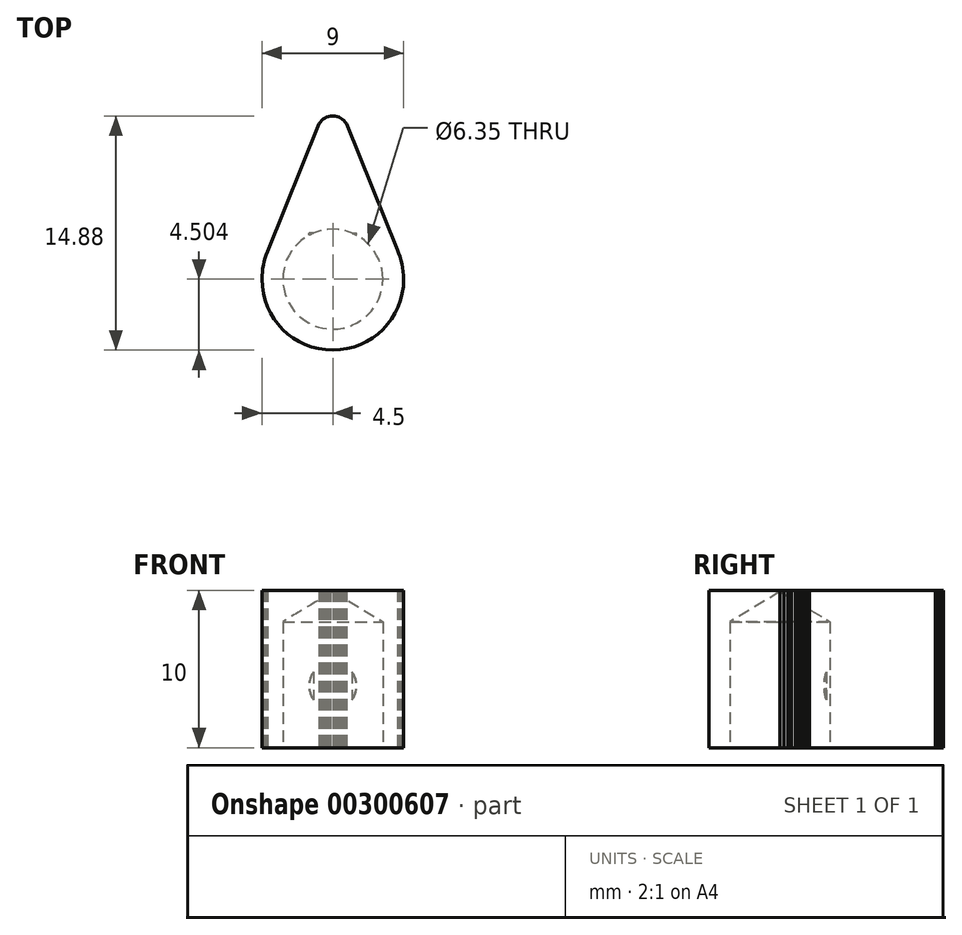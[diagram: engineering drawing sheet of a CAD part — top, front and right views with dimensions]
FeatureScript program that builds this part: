
annotation { "Feature Type Name" : "Feature", "Feature Type Description" : "" }
export const myFeature = defineFeature(function(context is Context, id is Id, definition is map)
    precondition{}
    {
        {
            var Q0;
            Q0=qCreatedBy(makeId("Top.planeOp"),FACE);
            var sketch = newSketch(context, id + "F0", { "sketchPlane" : qUnion([Q0])});
            skArc(sketch, "E0", {"start": v(0, 0.06) * mm, "mid": v(-2.12, -0.81) * mm, "end": v(-3, -2.94) * mm});
            skArc(sketch, "E1", {"start": v(-3, -2.94) * mm, "mid": v(-2.12, -5.06) * mm, "end": v(0, -5.94) * mm});
            skArc(sketch, "E2", {"start": v(0, -5.94) * mm, "mid": v(2.12, -5.06) * mm, "end": v(3, -2.94) * mm});
            skArc(sketch, "E3", {"start": v(3, -2.94) * mm, "mid": v(2.12, -0.81) * mm, "end": v(0, 0.06) * mm});
            skLineSegment(sketch, "E4", {"start": v(-0.86, 6.94) * mm, "end": v(-0.8, 7.05) * mm});
            skLineSegment(sketch, "E5", {"start": v(-0.8, 7.05) * mm, "end": v(-0.7, 7.14) * mm});
            skLineSegment(sketch, "E6", {"start": v(-0.7, 7.14) * mm, "end": v(-0.61, 7.23) * mm});
            skLineSegment(sketch, "E7", {"start": v(-0.61, 7.23) * mm, "end": v(-0.5, 7.3) * mm});
            skLineSegment(sketch, "E8", {"start": v(-0.5, 7.3) * mm, "end": v(-0.4, 7.36) * mm});
            skLineSegment(sketch, "E9", {"start": v(-0.4, 7.36) * mm, "end": v(-0.27, 7.4) * mm});
            skLineSegment(sketch, "E10", {"start": v(-0.27, 7.4) * mm, "end": v(-0.14, 7.43) * mm});
            skLineSegment(sketch, "E11", {"start": v(-0.14, 7.43) * mm, "end": v(0, 7.44) * mm});
            skLineSegment(sketch, "E12", {"start": v(0, 7.44) * mm, "end": v(0.13, 7.43) * mm});
            skLineSegment(sketch, "E13", {"start": v(0.13, 7.43) * mm, "end": v(0.26, 7.4) * mm});
            skLineSegment(sketch, "E14", {"start": v(0.26, 7.4) * mm, "end": v(0.38, 7.36) * mm});
            skLineSegment(sketch, "E15", {"start": v(0.38, 7.36) * mm, "end": v(0.5, 7.3) * mm});
            skLineSegment(sketch, "E16", {"start": v(0.5, 7.3) * mm, "end": v(0.6, 7.23) * mm});
            skLineSegment(sketch, "E17", {"start": v(0.6, 7.23) * mm, "end": v(0.7, 7.15) * mm});
            skLineSegment(sketch, "E18", {"start": v(0.7, 7.15) * mm, "end": v(0.78, 7.06) * mm});
            skLineSegment(sketch, "E19", {"start": v(0.78, 7.06) * mm, "end": v(0.86, 6.95) * mm});
            skLineSegment(sketch, "E20", {"start": v(0.86, 6.95) * mm, "end": v(4.1, -1.07) * mm});
            skLineSegment(sketch, "E21", {"start": v(4.1, -1.07) * mm, "end": v(4.19, -1.29) * mm});
            skLineSegment(sketch, "E22", {"start": v(4.19, -1.29) * mm, "end": v(4.27, -1.51) * mm});
            skLineSegment(sketch, "E23", {"start": v(4.27, -1.51) * mm, "end": v(4.34, -1.74) * mm});
            skLineSegment(sketch, "E24", {"start": v(4.34, -1.74) * mm, "end": v(4.4, -1.97) * mm});
            skLineSegment(sketch, "E25", {"start": v(4.4, -1.97) * mm, "end": v(4.44, -2.2) * mm});
            skLineSegment(sketch, "E26", {"start": v(4.44, -2.2) * mm, "end": v(4.47, -2.45) * mm});
            skLineSegment(sketch, "E27", {"start": v(4.47, -2.45) * mm, "end": v(4.5, -2.69) * mm});
            skLineSegment(sketch, "E28", {"start": v(4.5, -2.69) * mm, "end": v(4.5, -2.94) * mm});
            skArc(sketch, "E29", {"start": v(4.5, -2.94) * mm, "mid": v(3.18, -6.12) * mm, "end": v(0, -7.44) * mm});
            skArc(sketch, "E30", {"start": v(0, -7.44) * mm, "mid": v(-3.18, -6.12) * mm, "end": v(-4.5, -2.94) * mm});
            skLineSegment(sketch, "E31", {"start": v(-4.5, -2.94) * mm, "end": v(-4.5, -2.7) * mm});
            skLineSegment(sketch, "E32", {"start": v(-4.5, -2.7) * mm, "end": v(-4.48, -2.48) * mm});
            skLineSegment(sketch, "E33", {"start": v(-4.48, -2.48) * mm, "end": v(-4.45, -2.26) * mm});
            skLineSegment(sketch, "E34", {"start": v(-4.45, -2.26) * mm, "end": v(-4.4, -2.03) * mm});
            skLineSegment(sketch, "E35", {"start": v(-4.4, -2.03) * mm, "end": v(-4.36, -1.82) * mm});
            skLineSegment(sketch, "E36", {"start": v(-4.36, -1.82) * mm, "end": v(-4.3, -1.6) * mm});
            skLineSegment(sketch, "E37", {"start": v(-4.3, -1.6) * mm, "end": v(-4.23, -1.4) * mm});
            skLineSegment(sketch, "E38", {"start": v(-4.23, -1.4) * mm, "end": v(-4.15, -1.2) * mm});
            skLineSegment(sketch, "E39", {"start": v(-4.15, -1.2) * mm, "end": v(-0.86, 6.94) * mm});
            skSolve(sketch);
        }
        {
            var Q0;
            Q0=makeQuery(id+"F0.imprint","IMPRINT",FACE,{"disambiguationData":[TD([[makeQuery(id+"F0.imprint","IMPRINT",EDGE,{"derivedFrom":sQuery(id+"F0.wireOp",EDGE,"E0")}),-1.0]])]});
            extrude(context, id + "F1", {"entities" : qUnion([Q0]), "depth" : 10 * mm});
        }
        {
            var Q0;
            Q0=makeQuery(id+"F0.imprint","IMPRINT",FACE,{"disambiguationData":[TD([[makeQuery(id+"F0.imprint","IMPRINT",EDGE,{"derivedFrom":sQuery(id+"F0.wireOp",EDGE,"E0")}),1.0]])]});
            extrude(context, id + "F2", {"entities" : qUnion([Q0]), "operationType" : NewBodyOperationType.ADD, "depth" : 10 * mm});
        }
        {
            var Q0;
            Q0=sQuery(id+"F0.wireOp",VERTEX,"E0.center");
            var Q1;
            Q1=makeQuery(id+"F1.opExtrude","SWEPT_BODY",BODY,{"disambiguationData":[OSD([sQuery(id+"F0.wireOp",EDGE,"E0"),sQuery(id+"F0.wireOp",EDGE,"E1"),sQuery(id+"F0.wireOp",EDGE,"E2"),sQuery(id+"F0.wireOp",EDGE,"E3"),sQuery(id+"F0.wireOp",EDGE,"E4"),sQuery(id+"F0.wireOp",EDGE,"E5"),sQuery(id+"F0.wireOp",EDGE,"E6"),sQuery(id+"F0.wireOp",EDGE,"E7"),sQuery(id+"F0.wireOp",EDGE,"E8"),sQuery(id+"F0.wireOp",EDGE,"E9"),sQuery(id+"F0.wireOp",EDGE,"E10"),sQuery(id+"F0.wireOp",EDGE,"E11"),sQuery(id+"F0.wireOp",EDGE,"E12"),sQuery(id+"F0.wireOp",EDGE,"E13"),sQuery(id+"F0.wireOp",EDGE,"E14"),sQuery(id+"F0.wireOp",EDGE,"E15"),sQuery(id+"F0.wireOp",EDGE,"E16"),sQuery(id+"F0.wireOp",EDGE,"E17"),sQuery(id+"F0.wireOp",EDGE,"E18"),sQuery(id+"F0.wireOp",EDGE,"E19"),sQuery(id+"F0.wireOp",EDGE,"E20"),sQuery(id+"F0.wireOp",EDGE,"E21"),sQuery(id+"F0.wireOp",EDGE,"E22"),sQuery(id+"F0.wireOp",EDGE,"E23"),sQuery(id+"F0.wireOp",EDGE,"E24"),sQuery(id+"F0.wireOp",EDGE,"E25"),sQuery(id+"F0.wireOp",EDGE,"E26"),sQuery(id+"F0.wireOp",EDGE,"E27"),sQuery(id+"F0.wireOp",EDGE,"E28"),sQuery(id+"F0.wireOp",EDGE,"E29"),sQuery(id+"F0.wireOp",EDGE,"E30"),sQuery(id+"F0.wireOp",EDGE,"E31"),sQuery(id+"F0.wireOp",EDGE,"E32"),sQuery(id+"F0.wireOp",EDGE,"E33"),sQuery(id+"F0.wireOp",EDGE,"E34"),sQuery(id+"F0.wireOp",EDGE,"E35"),sQuery(id+"F0.wireOp",EDGE,"E36"),sQuery(id+"F0.wireOp",EDGE,"E37"),sQuery(id+"F0.wireOp",EDGE,"E38"),sQuery(id+"F0.wireOp",EDGE,"E39")])]});
            hole(context, id + "F3", {"style" : HoleStyle.SIMPLE, "endStyle" : HoleEndStyle.BLIND, "oppositeDirection" : true, "holeDiameter" : 6.35 * mm, "holeDepth" : 8 * mm, "tappedDepth" : 12 * mm, "tapClearance" : 3, "locations" : qUnion([Q0]), "scope" : qUnion([Q1])});
        }
        {
            var Q0;
            Q0=qCreatedBy(makeId("Front.planeOp"),FACE);
            var sketch = newSketch(context, id + "F4", { "sketchPlane" : qUnion([Q0])});
            skCircle(sketch, "E40", {"center": v(0, 3.93) * mm, "radius": 1.53 * mm});
            skSolve(sketch);
        }
        {
            var Q0;
            Q0=sQuery(id+"F4.wireOp",VERTEX,"E40.center");
            var Q1;
            Q1=makeQuery(id+"F1.opExtrude","SWEPT_BODY",BODY,{"disambiguationData":[OSD([sQuery(id+"F0.wireOp",EDGE,"E0"),sQuery(id+"F0.wireOp",EDGE,"E1"),sQuery(id+"F0.wireOp",EDGE,"E2"),sQuery(id+"F0.wireOp",EDGE,"E3"),sQuery(id+"F0.wireOp",EDGE,"E4"),sQuery(id+"F0.wireOp",EDGE,"E5"),sQuery(id+"F0.wireOp",EDGE,"E6"),sQuery(id+"F0.wireOp",EDGE,"E7"),sQuery(id+"F0.wireOp",EDGE,"E8"),sQuery(id+"F0.wireOp",EDGE,"E9"),sQuery(id+"F0.wireOp",EDGE,"E10"),sQuery(id+"F0.wireOp",EDGE,"E11"),sQuery(id+"F0.wireOp",EDGE,"E12"),sQuery(id+"F0.wireOp",EDGE,"E13"),sQuery(id+"F0.wireOp",EDGE,"E14"),sQuery(id+"F0.wireOp",EDGE,"E15"),sQuery(id+"F0.wireOp",EDGE,"E16"),sQuery(id+"F0.wireOp",EDGE,"E17"),sQuery(id+"F0.wireOp",EDGE,"E18"),sQuery(id+"F0.wireOp",EDGE,"E19"),sQuery(id+"F0.wireOp",EDGE,"E20"),sQuery(id+"F0.wireOp",EDGE,"E21"),sQuery(id+"F0.wireOp",EDGE,"E22"),sQuery(id+"F0.wireOp",EDGE,"E23"),sQuery(id+"F0.wireOp",EDGE,"E24"),sQuery(id+"F0.wireOp",EDGE,"E25"),sQuery(id+"F0.wireOp",EDGE,"E26"),sQuery(id+"F0.wireOp",EDGE,"E27"),sQuery(id+"F0.wireOp",EDGE,"E28"),sQuery(id+"F0.wireOp",EDGE,"E29"),sQuery(id+"F0.wireOp",EDGE,"E30"),sQuery(id+"F0.wireOp",EDGE,"E31"),sQuery(id+"F0.wireOp",EDGE,"E32"),sQuery(id+"F0.wireOp",EDGE,"E33"),sQuery(id+"F0.wireOp",EDGE,"E34"),sQuery(id+"F0.wireOp",EDGE,"E35"),sQuery(id+"F0.wireOp",EDGE,"E36"),sQuery(id+"F0.wireOp",EDGE,"E37"),sQuery(id+"F0.wireOp",EDGE,"E38"),sQuery(id+"F0.wireOp",EDGE,"E39")])]});
            hole(context, id + "F5", {"style" : HoleStyle.SIMPLE, "endStyle" : HoleEndStyle.BLIND, "oppositeDirection" : true, "holeDiameter" : 3 * mm, "holeDepth" : 5 * mm, "tappedDepth" : 12 * mm, "tapClearance" : 3, "locations" : qUnion([Q0]), "scope" : qUnion([Q1])});
        }
    });
